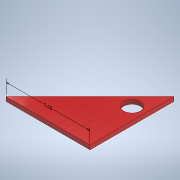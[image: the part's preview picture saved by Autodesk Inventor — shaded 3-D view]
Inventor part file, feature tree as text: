
AUTODESK INVENTOR PART (.ipt)
format: ipt  version: 2021.1 (Build 251245010, 245A)  size: 115,712 bytes
history: native  units: in
note: dims shown in document units (in); Inventor stores cm internally (conversion verified against a paired STEP export)
features: other x2, sketch x2, extrude x1, hole x1
ambient origin geometry x8: Origin, YZ Plane, XZ Plane, XY Plane, X Axis, Y Axis, Z Axis, Center Point
bodies: Solid1 (feature_tree)
feature tree (6):
  other  "Annotations"
  extrude  "Extrusion1"  TaperAngle=45.0deg  [1 undecoded]
  hole  "Hole1"  [1 undecoded]
  sketch  "Sketch1"  dims[d0=5.0in d1=45.0deg]
  sketch  "Sketch2"  dims[d5=0.25in d6=0.0in d9=0.75in d11=1.0in d12=0.75in d13=0.375in d14=0.25in d15=0.5635in d16=0.575in d17=0.0in d21=1.75in d22=0.0in d23=0.3937in d24=5.0in]
  other  "Linear Dimension 1"
note: 2 required parameter values undecoded (feature->parameter linkage not recoverable at this tier; creation-order binding heuristic only, values carry confidence <= 0.55)
